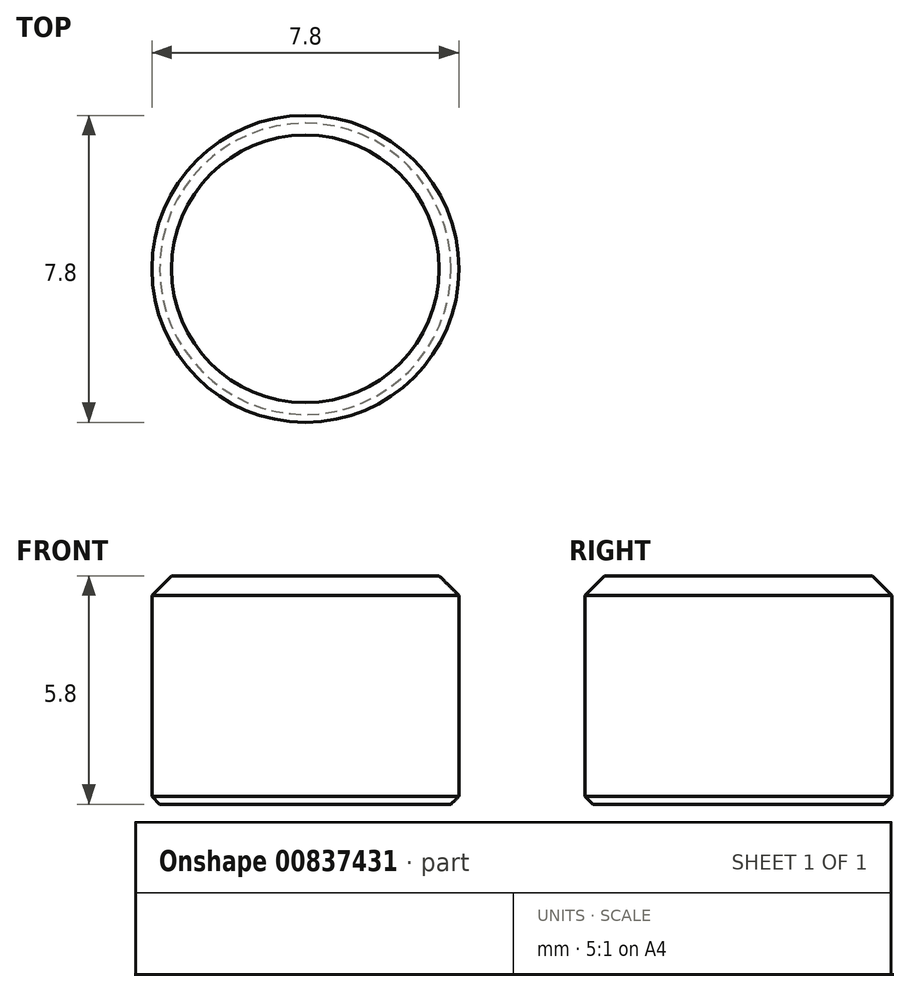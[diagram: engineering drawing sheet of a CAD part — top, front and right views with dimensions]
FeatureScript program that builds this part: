
annotation { "Feature Type Name" : "Feature", "Feature Type Description" : "" }
export const myFeature = defineFeature(function(context is Context, id is Id, definition is map)
    precondition{}
    {
        {
            var Q0;
            Q0=qCreatedBy(makeId("Top.planeOp"),FACE);
            var sketch = newSketch(context, id + "F0", { "sketchPlane" : qUnion([Q0])});
            skCircle(sketch, "E0", {"center": v(0, 0) * mm, "radius": 3.9 * mm});
            skSolve(sketch);
        }
        {
            var Q0;
            Q0=makeQuery(id+"F0.imprint","IMPRINT",FACE,{"disambiguationData":[TD([[makeQuery(id+"F0.imprint","IMPRINT",EDGE,{"derivedFrom":sQuery(id+"F0.wireOp",EDGE,"E0")}),1.0]])]});
            extrude(context, id + "F1", {"entities" : qUnion([Q0]), "depth" : 5.8 * mm, "offsetDistance" : 25 * mm});
        }
        {
            var Q0;
            Q0=makeQuery(id+"F1.opExtrude","CAP_EDGE",EDGE,{"disambiguationData":[OSD([sQuery(id+"F0.wireOp",EDGE,"E0")])],"isStart":false});
            chamfer(context, id + "F2", {"entities" : qUnion([Q0]), "width" : .5 * mm, "tangentPropagation" : true});
        }
        {
            var Q0;
            Q0=makeQuery(id+"F1.opExtrude","CAP_EDGE",EDGE,{"disambiguationData":[OSD([sQuery(id+"F0.wireOp",EDGE,"E0")])],"isStart":true});
            chamfer(context, id + "F3", {"entities" : qUnion([Q0]), "width" : .2 * mm, "tangentPropagation" : true});
        }
    });
